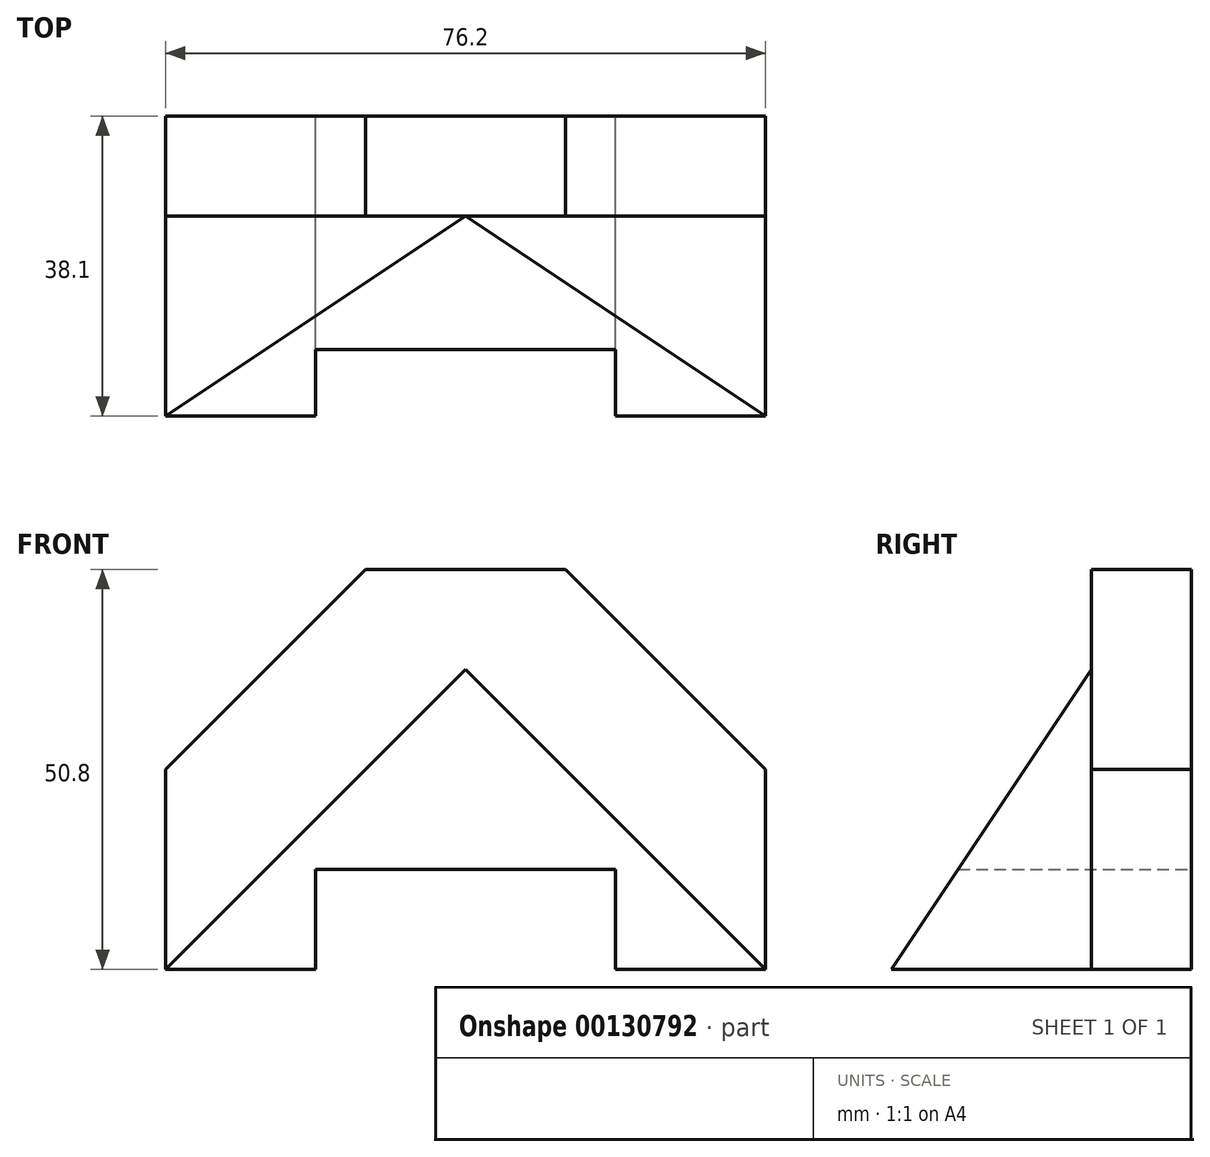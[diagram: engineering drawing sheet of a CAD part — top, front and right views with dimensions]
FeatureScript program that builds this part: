
annotation { "Feature Type Name" : "Feature", "Feature Type Description" : "" }
export const myFeature = defineFeature(function(context is Context, id is Id, definition is map)
    precondition{}
    {
        {
            var Q0;
            Q0=qCreatedBy(makeId("Front.planeOp"),FACE);
            var sketch = newSketch(context, id + "F0", { "sketchPlane" : qUnion([Q0])});
            skLineSegment(sketch, "E0.bottom", {"start": v(0, 0) * mm, "end": v(76.2, 0) * mm});
            skLineSegment(sketch, "E0.top", {"start": v(0, 50.8) * mm, "end": v(76.2, 50.8) * mm});
            skLineSegment(sketch, "E0.left", {"start": v(0, 0) * mm, "end": v(0, 50.8) * mm});
            skLineSegment(sketch, "E0.right", {"start": v(76.2, 0) * mm, "end": v(76.2, 50.8) * mm});
            skLineSegment(sketch, "E1", {"start": v(38.1, 0) * mm, "end": v(38.1, 38.1) * mm, "construction": true});
            skLineSegment(sketch, "E2", {"start": v(0, 0) * mm, "end": v(38.1, 38.1) * mm});
            skLineSegment(sketch, "E3", {"start": v(38.1, 38.1) * mm, "end": v(76.2, 0) * mm});
            skLineSegment(sketch, "E4", {"start": v(0, 25.4) * mm, "end": v(25.4, 50.8) * mm});
            skLineSegment(sketch, "E5", {"start": v(76.2, 25.4) * mm, "end": v(50.8, 50.8) * mm});
            skLineSegment(sketch, "E6.bottom", {"start": v(19.05, 0) * mm, "end": v(57.15, 0) * mm});
            skLineSegment(sketch, "E6.top", {"start": v(19.05, 12.7) * mm, "end": v(57.15, 12.7) * mm});
            skLineSegment(sketch, "E6.left", {"start": v(19.05, 0) * mm, "end": v(19.05, 12.7) * mm});
            skLineSegment(sketch, "E6.right", {"start": v(57.15, 0) * mm, "end": v(57.15, 12.7) * mm});
            skSolve(sketch);
        }
        {
            var Q0;
            {var subQ0=sQuery(id+"F0.wireOp",EDGE,"E2");Q0=makeQuery(id+"F0.imprint","IMPRINT",FACE,{"disambiguationData":[TD([[makeQuery(id+"F0.imprint","IMPRINT",EDGE,{"derivedFrom":subQ0}),1.0]])]});}
            extrude(context, id + "F1", {"entities" : qUnion([Q0]), "depth" : 12.7 * mm});
        }
        {
            var Q0;
            {var subQ1=sQuery(id+"F0.wireOp",EDGE,"E2");Q0=makeQuery(id+"F0.imprint","IMPRINT",FACE,{"disambiguationData":[TD([[makeQuery(id+"F0.imprint","IMPRINT",EDGE,{"derivedFrom":subQ1}),-1.0]])]});}
            extrude(context, id + "F2", {"entities" : qUnion([Q0]), "operationType" : NewBodyOperationType.ADD, "depth" : 38.1 * mm});
        }
        {
            var Q0;
            Q0=qCreatedBy(makeId("Right.planeOp"),FACE);
            var sketch = newSketch(context, id + "F3", { "sketchPlane" : qUnion([Q0])});
            skLineSegment(sketch, "E7", {"start": v(-38.1, 38.1) * mm, "end": v(-12.7, 38.1) * mm});
            skLineSegment(sketch, "E8", {"start": v(-12.7, 38.1) * mm, "end": v(-38.1, 0) * mm});
            skLineSegment(sketch, "E9", {"start": v(-38.1, 38.1) * mm, "end": v(-38.1, 0) * mm});
            skSolve(sketch);
        }
        {
            var Q0;
            Q0 = qSketchRegion(id + "F3", true);
            extrude(context, id + "F4", {"entities" : qUnion([Q0]), "operationType" : NewBodyOperationType.REMOVE, "depth" : 76.2 * mm});
        }
    });
